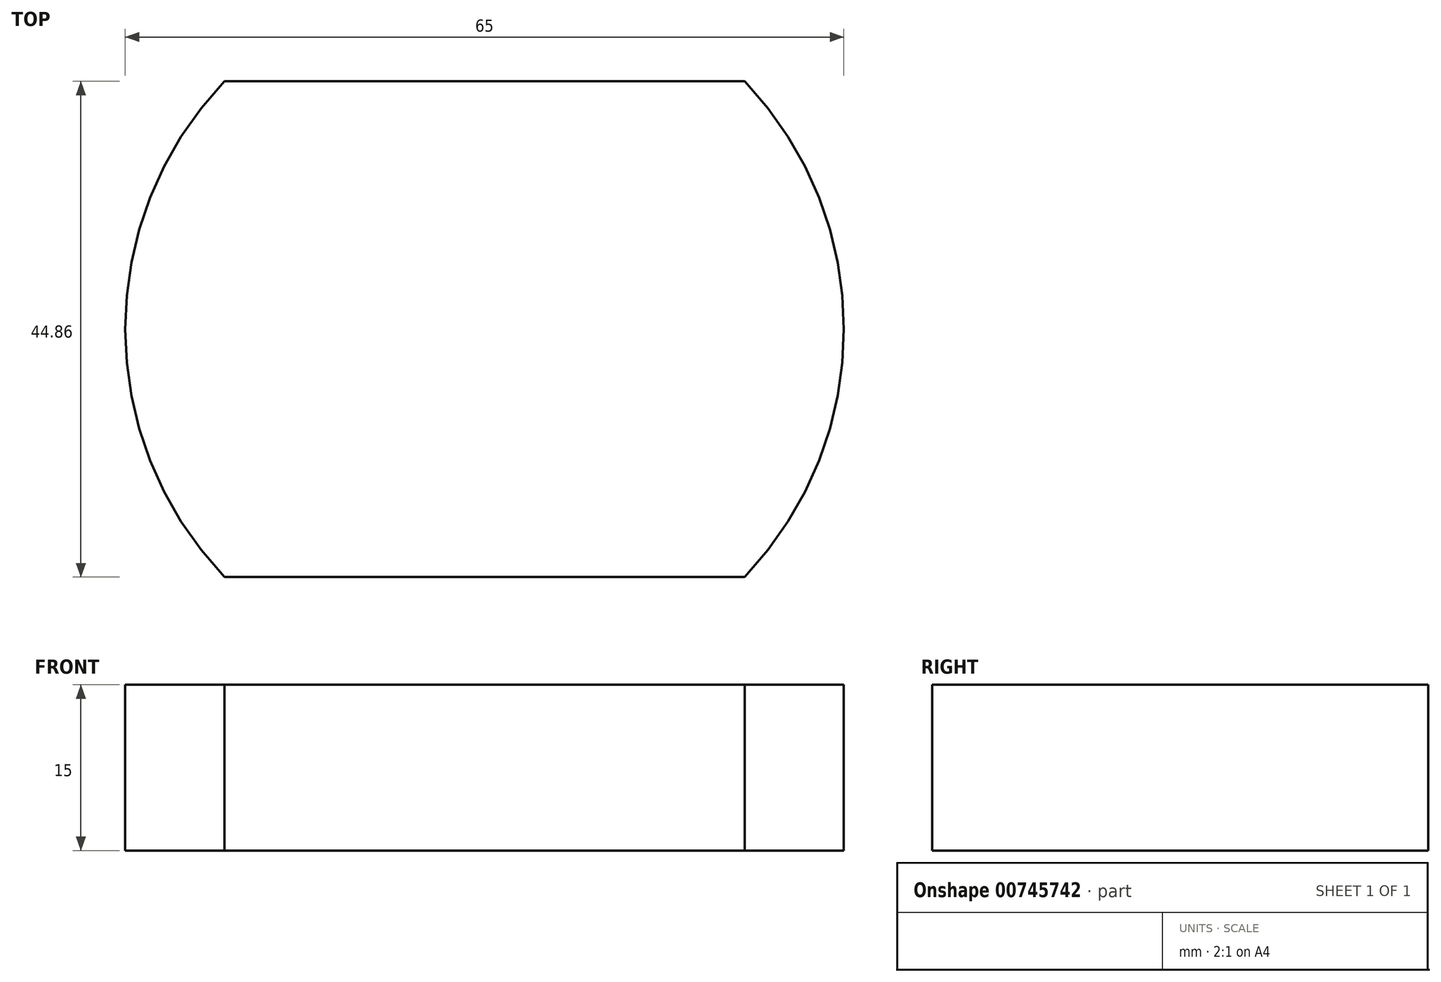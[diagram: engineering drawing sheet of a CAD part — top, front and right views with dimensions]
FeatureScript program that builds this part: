
annotation { "Feature Type Name" : "Feature", "Feature Type Description" : "" }
export const myFeature = defineFeature(function(context is Context, id is Id, definition is map)
    precondition{}
    {
        {
            var Q0;
            Q0=qCreatedBy(makeId("Top.planeOp"),FACE);
            var sketch = newSketch(context, id + "F0", { "sketchPlane" : qUnion([Q0])});
            skArc(sketch, "E0", {"start": v(-24.42, 17.43) * mm, "mid": v(-30, 0) * mm, "end": v(-24.42, -17.43) * mm});
            skLineSegment(sketch, "E1", {"start": v(-24.42, -17.43) * mm, "end": v(24.42, -17.43) * mm});
            skLineSegment(sketch, "E2", {"start": v(-24.42, 17.43) * mm, "end": v(24.42, 17.43) * mm});
            skArc(sketch, "E3.trimOffspring", {"start": v(24.42, -17.43) * mm, "mid": v(30, 0) * mm, "end": v(24.42, 17.43) * mm});
            skSolve(sketch);
        }
        {
            var Q0;
            Q0 = qSketchRegion(id + "F0", true);
            extrude(context, id + "F1", {"entities" : qUnion([Q0]), "depth" : 10 * mm, "offsetDistance" : 25.4 * mm});
        }
        {
            var Q0;
            Q0=qCreatedBy(makeId("Top.planeOp"),FACE);
            var sketch = newSketch(context, id + "F2", { "sketchPlane" : qUnion([Q0])});
            skArc(sketch, "E4", {"start": v(23.52, -22.43) * mm, "mid": v(32.5, 0) * mm, "end": v(23.52, 22.43) * mm});
            skLineSegment(sketch, "E5", {"start": v(-23.52, -22.43) * mm, "end": v(23.52, -22.43) * mm});
            skLineSegment(sketch, "E6", {"start": v(-23.52, 22.43) * mm, "end": v(23.52, 22.43) * mm});
            skArc(sketch, "E7.trimOffspring", {"start": v(-23.52, 22.43) * mm, "mid": v(-32.5, 0) * mm, "end": v(-23.52, -22.43) * mm});
            skSolve(sketch);
        }
        {
            var Q0;
            Q0 = qSketchRegion(id + "F2", true);
            extrude(context, id + "F3", {"entities" : qUnion([Q0]), "operationType" : NewBodyOperationType.ADD, "depth" : 15 * mm, "offsetDistance" : 25.4 * mm});
        }
    });
